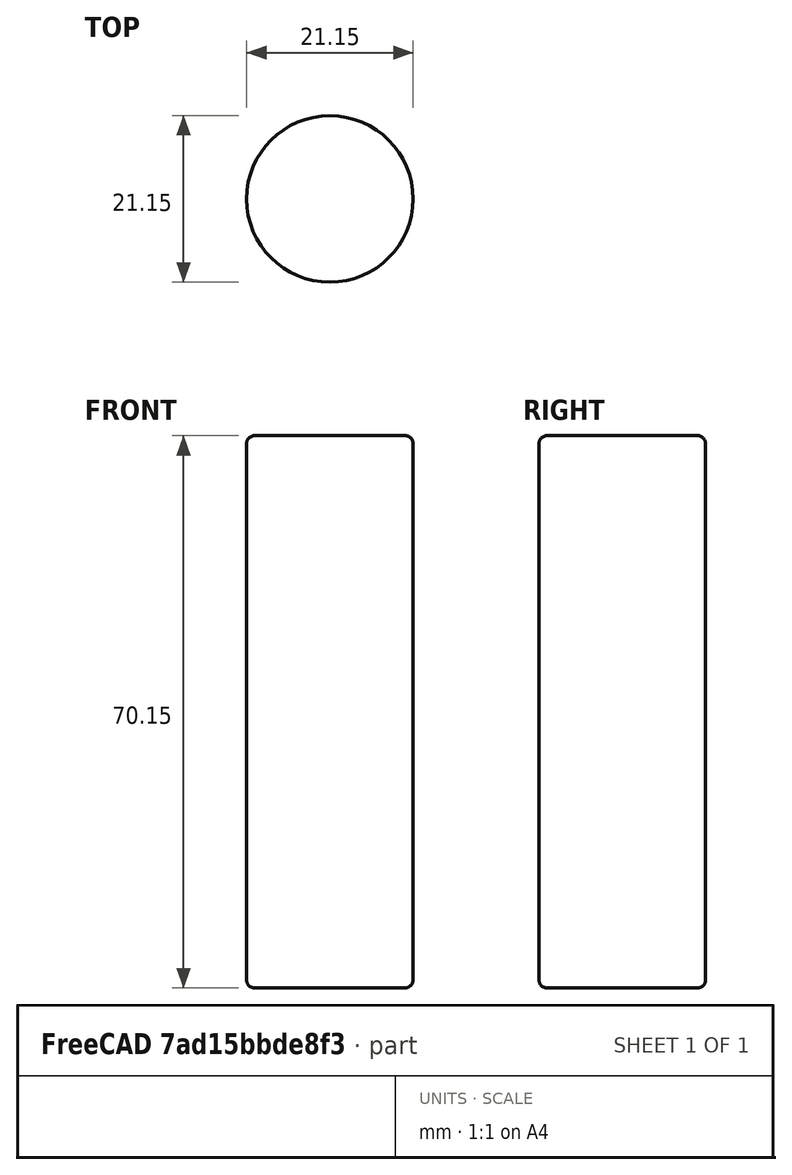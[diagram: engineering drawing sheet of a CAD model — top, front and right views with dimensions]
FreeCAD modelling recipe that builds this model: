
FCSTD DOCUMENT  (FreeCAD 1.0R39109 (Git))
Label: pile
License: All rights reserved
LicenseURL: http://en.wikipedia.org/wiki/All_rights_reserved
objects: Sketcher::SketchObject×1, PartDesign::Pad×1, PartDesign::Fillet×1, PartDesign::Body×1
note: 9 computed .brp shape members not serialized (recipe doc carries the construction recipe); baked Part::Feature solids carry a one-line shape summary decoded from their .brp

FEATURE [Sketcher::SketchObject] Sketch
  ArcFitTolerance = 0
  AttachmentSupport = -> [XY_Plane]
  FullyConstrained = true
  MakeInternals = false
  MapMode = 5
  sketch-geometry (1):
    g0: Circle CenterX=0 CenterY=0 CenterZ=0 NormalX=0 NormalY=0 NormalZ=1 AngleXU=0 Radius=10.575
  constraints (2):
    c: Coincident(g0,g-1)
    c: Diameter(g0) = 21.15
FEATURE [PartDesign::Pad] Pad
  Direction = (0,0,1)
  Length = 70.15
  Length2 = 10
  Profile = -> Sketch
  ReferenceAxis = -> Sketch [N_Axis]
  Suppressed = false
  Type = 0
FEATURE [PartDesign::Fillet] Fillet
  Base = -> Pad [Edge3,Edge2]
  BaseFeature = -> Pad
  Radius = 1
  SupportTransform = false
  Suppressed = false
  UseAllEdges = false
FEATURE [PartDesign::Body] Body  label="Corps"
  AllowCompound = false
  Group = -> [Sketch,Pad,Fillet]
  Origin = -> Origin
  Tip = -> Fillet
